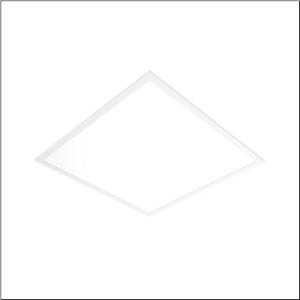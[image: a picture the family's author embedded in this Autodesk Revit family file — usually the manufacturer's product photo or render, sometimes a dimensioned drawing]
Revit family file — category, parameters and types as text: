
# Revit family: apollon_r__41_51mh11w72343_11b4
name_source: partatom
category: Lighting Fixtures
units: mm (PartAtom-declared; Revit-internal decimal feet)

## family parameters
Cut with Voids When Loaded = No
Host = Face
Light Source = No
Part Type = Normal
Room Calculation Point = No
Round Connector Dimension = Use Diameter
Shared = No

## types (1)
- Apollon® 41 (1 x LED, 3500 lm, 28.5 W, 3000K)
    Apparent Load = 29 VA
    CIE Flux Codes = 61 87 97 100 100
    Color Rendering = 80
    Color Temperature = 3000K
    Default Elevation = 1800 mm
    Description = Apollon® 41, office luminaire, primary optical cover: prismatic diffuser, of PS, light emission: direct distribution, primary light characteristic: symmetric, installation type: lay-in mounting, LED, rated luminous flux: 3.500lm, luminous efficacy: 123lm/W, light colour: 830, colour temperature: 3000K, with terminal, 3-pole, mains connection: 220..240V, AC, 50/60Hz, housing, of aluminium section, traffic white (RAL 9016), module: M625, length: 620mm, width: 620mm, height: 40mm, housing upper side, of sheet steel, protection rating (complete): IP20, protection rating (lamp compartment, on room side): IP40, insulation class (complete): insulation class II (safety insulation), certification: CE, ENEC, permissible operating ambient temperature: -20..+40°C, packaging unit: 1 piece
    Height = 0 mm  [stored 0 ft]
    Lamp = 1 x LED
    Lamp Light Flux = 3500 lm
    Lamp Power = 28.5 W
    Lamp count = 1
    Length = 620 mm
    Luminous efficacy = 123 lm/W
    Manufacturer = Siteco
    ModVariant = No
    Model = 51MH11W72343
    Mounting Place = Ceiling
    Mounting Type = Recessed
    Number of Poles = 1
    OnlyDefault = Yes
    Power Factor = 1
    Product Name = Apollon® 41
    Product group = office luminaire | ceiling recessed
    ProductGroupID = 401
    Protection Class = Protection class II
    Protection Degree = IP 20
    RLX_Detail_Level = 1
    RLX_Emergency_Light_Flux = 0 lm
    RLX_Emergency_Type = 0
    RLX_Emergency_Type_DB = No
    RlxData = <blob elided: 12177 chars, md5=e789a620>
    Socket = socket
    Standby Power = 0 W
    System Light Flux = 3500 lm
    System Power = 29 W
    Type Comments = Product without accessories
    Type Image = l_1291024.jpg
    URL = http://relux.com
    VarID = ---
    Voltage = 0 V
    Weight = 0.00 kg
    Width = 620 mm

note: [stored X ft] marks values corroborated as IEEE doubles in the binary element streams (Revit-internal decimal feet)

## geometry (parser evidence)
native form markers: Sweep x8
no freeform markers — native parametric forms only
